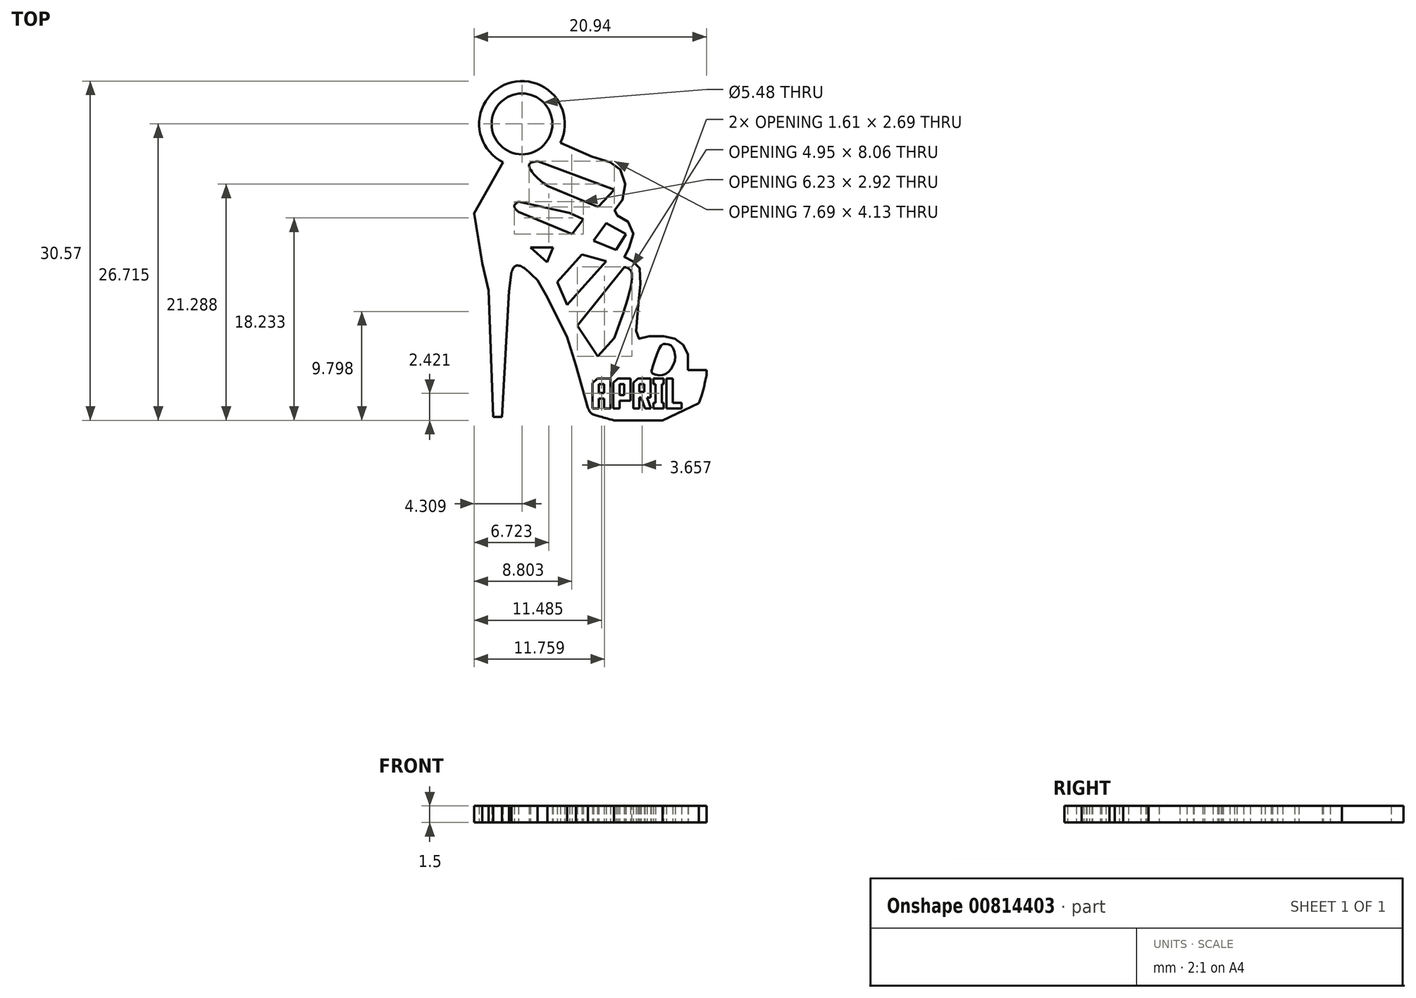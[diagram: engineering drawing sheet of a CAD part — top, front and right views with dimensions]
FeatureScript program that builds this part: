
annotation { "Feature Type Name" : "Feature", "Feature Type Description" : "" }
export const myFeature = defineFeature(function(context is Context, id is Id, definition is map)
    precondition{}
    {
        {
            var Q0;
            Q0=qCreatedBy(makeId("Top.planeOp"),FACE);
            var sketch = newSketch(context, id + "F0", { "sketchPlane" : qUnion([Q0])});
            skLineSegment(sketch, "E0", {"start": v(-16.68, 3.96) * mm, "end": v(-15.9, 3.96) * mm});
            skLineSegment(sketch, "E1", {"start": v(-15.9, 3.96) * mm, "end": v(-15.26, 15.28) * mm});
            skLineSegment(sketch, "E2", {"start": v(-15.26, 15.28) * mm, "end": v(-15.01, 17.04) * mm});
            skFitSpline(sketch, "E3", {"points": [v(-15.01, 17.04) * mm, v(-14.7, 17.54) * mm, v(-14.13, 17.51) * mm, v(-13.22, 16.79) * mm], "startDerivative": vector(0.84, 2.09) * mm, "endDerivative": vector(2.2, -2.1) * mm});
            skLineSegment(sketch, "E4", {"start": v(-13.22, 16.79) * mm, "end": v(-12.7, 16.29) * mm});
            skLineSegment(sketch, "E5", {"start": v(-12.7, 16.29) * mm, "end": v(-11.78, 14.72) * mm});
            skLineSegment(sketch, "E6", {"start": v(-11.78, 14.72) * mm, "end": v(-10.03, 11.14) * mm});
            skLineSegment(sketch, "E7", {"start": v(-10.03, 11.14) * mm, "end": v(-9.2, 8.6) * mm});
            skLineSegment(sketch, "E8", {"start": v(-9.2, 8.6) * mm, "end": v(-8.13, 4.75) * mm});
            skFitSpline(sketch, "E9", {"points": [v(-8.13, 4.75) * mm, v(-7.86, 4.3) * mm, v(-7.32, 4.07) * mm, v(-5.8, 3.65) * mm], "startDerivative": vector(0.86, -1.92) * mm, "endDerivative": vector(3.7, -1) * mm});
            skLineSegment(sketch, "E10", {"start": v(-5.8, 3.65) * mm, "end": v(-3.32, 3.65) * mm});
            skLineSegment(sketch, "E11", {"start": v(-3.32, 3.65) * mm, "end": v(-1.41, 3.65) * mm});
            skLineSegment(sketch, "E12", {"start": v(-1.41, 3.65) * mm, "end": v(0.53, 4.57) * mm});
            skLineSegment(sketch, "E13", {"start": v(0.53, 4.57) * mm, "end": v(1.87, 5.2) * mm});
            skLineSegment(sketch, "E14", {"start": v(2.55, 7.7) * mm, "end": v(2.55, 8.18) * mm});
            skLineSegment(sketch, "E15", {"start": v(2.55, 8.18) * mm, "end": v(0.87, 8.18) * mm});
            skFitSpline(sketch, "E16", {"points": [v(0.87, 8.95) * mm, v(0.87, 9.57) * mm, v(0.2, 10.71) * mm, v(-0.94, 11.17) * mm, v(-3.14, 11.12) * mm, v(-3.7, 11.05) * mm, v(-3.4, 16.13) * mm, v(-3.9, 17.9) * mm, v(-4.83, 18.34) * mm, v(-4.12, 19.88) * mm, v(-4.72, 21.75) * mm, v(-5.82, 22.35) * mm, v(-4.97, 23.62) * mm, v(-5.27, 26.34) * mm, v(-10.61, 28.67) * mm], "startDerivative": vector(2.17, 13.71) * mm, "endDerivative": vector(-80.97, 44.17) * mm});
            skLineSegment(sketch, "E17", {"start": v(-15.8, 26.9) * mm, "end": v(-18.4, 22.3) * mm});
            skLineSegment(sketch, "E18", {"start": v(-18.4, 22.3) * mm, "end": v(-17.67, 17.78) * mm});
            skLineSegment(sketch, "E19", {"start": v(-17.67, 17.78) * mm, "end": v(-17.1, 15.35) * mm});
            skLineSegment(sketch, "E20", {"start": v(-17.1, 15.35) * mm, "end": v(-16.68, 3.96) * mm});
            skLineSegment(sketch, "E21", {"start": v(-12.7, 27) * mm, "end": v(-5.74, 24.42) * mm});
            skLineSegment(sketch, "E22", {"start": v(-5.74, 24.42) * mm, "end": v(-7.22, 22.87) * mm});
            skLineSegment(sketch, "E23", {"start": v(-7.22, 22.87) * mm, "end": v(-11.82, 24.8) * mm});
            skFitSpline(sketch, "E24", {"points": [v(-11.82, 24.8) * mm, v(-13, 25.82) * mm, v(-13.43, 26.72) * mm, v(-12.7, 27) * mm], "startDerivative": vector(-3.15, 2.36) * mm, "endDerivative": vector(3.5, 0.55) * mm});
            skLineSegment(sketch, "E25", {"start": v(-9.78, 22.33) * mm, "end": v(-8.55, 21.75) * mm});
            skLineSegment(sketch, "E26", {"start": v(-8.55, 21.75) * mm, "end": v(-9.55, 20.42) * mm});
            skLineSegment(sketch, "E27", {"start": v(-9.55, 20.42) * mm, "end": v(-14.4, 22.43) * mm});
            skFitSpline(sketch, "E28", {"points": [v(-14.4, 22.43) * mm, v(-14.78, 22.96) * mm, v(-14.4, 23.34) * mm], "startDerivative": vector(-1.1, 1.06) * mm, "endDerivative": vector(1.14, 0.76) * mm});
            skLineSegment(sketch, "E29", {"start": v(-14.4, 23.34) * mm, "end": v(-9.78, 22.33) * mm});
            skLineSegment(sketch, "E30", {"start": v(-6.48, 21.42) * mm, "end": v(-7.62, 19.83) * mm});
            skLineSegment(sketch, "E31", {"start": v(-7.62, 19.83) * mm, "end": v(-5.6, 19) * mm});
            skLineSegment(sketch, "E32", {"start": v(-5.6, 19) * mm, "end": v(-4.72, 20.42) * mm});
            skLineSegment(sketch, "E33", {"start": v(-4.72, 20.42) * mm, "end": v(-6.48, 21.42) * mm});
            skLineSegment(sketch, "E34", {"start": v(-13.3, 19.22) * mm, "end": v(-11.29, 19.22) * mm});
            skLineSegment(sketch, "E35", {"start": v(-11.29, 19.22) * mm, "end": v(-11.83, 17.9) * mm});
            skLineSegment(sketch, "E36", {"start": v(-11.83, 17.9) * mm, "end": v(-13.3, 19.22) * mm});
            skLineSegment(sketch, "E37", {"start": v(-10.9, 16.13) * mm, "end": v(-8.69, 18.6) * mm});
            skLineSegment(sketch, "E38", {"start": v(-8.69, 18.6) * mm, "end": v(-6.48, 17.98) * mm});
            skLineSegment(sketch, "E39", {"start": v(-6.48, 17.98) * mm, "end": v(-10, 14.06) * mm});
            skLineSegment(sketch, "E40", {"start": v(-10, 14.06) * mm, "end": v(-10.9, 16.13) * mm});
            skLineSegment(sketch, "E41", {"start": v(-4.83, 17.48) * mm, "end": v(-9.1, 12.2) * mm});
            skLineSegment(sketch, "E42", {"start": v(-9.1, 12.2) * mm, "end": v(-7.24, 9.42) * mm});
            skLineSegment(sketch, "E43", {"start": v(-7.24, 9.42) * mm, "end": v(-5.76, 11.06) * mm});
            skFitSpline(sketch, "E44", {"points": [v(-5.76, 11.06) * mm, v(-4.21, 17) * mm, v(-4.83, 17.48) * mm], "startDerivative": vector(3.76, 10.36) * mm, "endDerivative": vector(-2.95, 0.99) * mm});
            skFitSpline(sketch, "E45", {"points": [v(-1.53, 10.4) * mm, v(-2.31, 8.42) * mm, v(-2.37, 7.92) * mm, v(-1.62, 7.7) * mm, v(-0.9, 8.01) * mm, v(-0.28, 9.14) * mm, v(-0.6, 10.35) * mm, v(-1.12, 10.54) * mm, v(-1.53, 10.4) * mm]});
            skArc(sketch, "E46", {"start": v(-10.61, 28.67) * mm, "mid": v(-15.32, 34.02) * mm, "end": v(-15.8, 26.9) * mm});
            skLineSegment(sketch, "E47", {"start": v(0.87, 8.95) * mm, "end": v(0.87, 8.18) * mm});
            skCircle(sketch, "E48", {"center": v(-14.08, 30.36) * mm, "radius": 2.74 * mm});
            skFitSpline(sketch, "E49", {"points": [v(1.87, 5.2) * mm, v(2.18, 6.1) * mm, v(2.55, 7.7) * mm], "startDerivative": vector(0.73, 1.92) * mm, "endDerivative": vector(0.65, 3.04) * mm});
            skSolve(sketch);
        }
        {
            var Q0;
            Q0=qCreatedBy(makeId("Top.planeOp"),FACE);
            var sketch = newSketch(context, id + "F1", { "sketchPlane" : qUnion([Q0])});
            skLineSegment(sketch, "E50", {"start": v(-7.14, 4.73) * mm, "end": v(-7.7, 4.73) * mm});
            skLineSegment(sketch, "E51", {"start": v(-7.7, 4.73) * mm, "end": v(-7.7, 6.99) * mm});
            skLineSegment(sketch, "E52", {"start": v(-7.7, 6.99) * mm, "end": v(-7.28, 7.41) * mm});
            skLineSegment(sketch, "E53", {"start": v(-7.28, 7.41) * mm, "end": v(-6.1, 7.41) * mm});
            skLineSegment(sketch, "E54", {"start": v(-6.1, 7.41) * mm, "end": v(-6.1, 4.73) * mm});
            skLineSegment(sketch, "E55", {"start": v(-6.1, 4.73) * mm, "end": v(-6.66, 4.73) * mm});
            skLineSegment(sketch, "E56", {"start": v(-6.66, 4.73) * mm, "end": v(-6.66, 5.6) * mm});
            skLineSegment(sketch, "E57", {"start": v(-6.66, 5.6) * mm, "end": v(-7.14, 5.6) * mm});
            skLineSegment(sketch, "E58", {"start": v(-7.14, 5.6) * mm, "end": v(-7.14, 4.73) * mm});
            skLineSegment(sketch, "E59", {"start": v(-6.66, 6.12) * mm, "end": v(-6.66, 6.9) * mm});
            skLineSegment(sketch, "E60", {"start": v(-6.66, 6.9) * mm, "end": v(-7.14, 6.9) * mm});
            skLineSegment(sketch, "E61", {"start": v(-7.14, 6.9) * mm, "end": v(-7.14, 6.12) * mm});
            skLineSegment(sketch, "E62", {"start": v(-7.14, 6.12) * mm, "end": v(-6.66, 6.12) * mm});
            skLineSegment(sketch, "E63", {"start": v(-5.29, 4.73) * mm, "end": v(-5.85, 4.73) * mm});
            skLineSegment(sketch, "E64", {"start": v(-5.85, 4.73) * mm, "end": v(-5.85, 7.03) * mm});
            skLineSegment(sketch, "E65", {"start": v(-5.85, 7.03) * mm, "end": v(-5.44, 7.41) * mm});
            skLineSegment(sketch, "E66", {"start": v(-5.44, 7.41) * mm, "end": v(-4.3, 7.41) * mm});
            skLineSegment(sketch, "E67", {"start": v(-4.3, 7.41) * mm, "end": v(-4.3, 5.4) * mm});
            skLineSegment(sketch, "E68", {"start": v(-4.3, 5.4) * mm, "end": v(-5.29, 5.4) * mm});
            skLineSegment(sketch, "E69", {"start": v(-5.29, 5.4) * mm, "end": v(-5.29, 4.73) * mm});
            skLineSegment(sketch, "E70", {"start": v(-4.86, 5.92) * mm, "end": v(-4.86, 6.9) * mm});
            skLineSegment(sketch, "E71", {"start": v(-4.86, 6.9) * mm, "end": v(-5.29, 6.9) * mm});
            skLineSegment(sketch, "E72", {"start": v(-5.29, 6.9) * mm, "end": v(-5.29, 5.92) * mm});
            skLineSegment(sketch, "E73", {"start": v(-5.29, 5.92) * mm, "end": v(-4.86, 5.92) * mm});
            skLineSegment(sketch, "E74", {"start": v(-3, 4.73) * mm, "end": v(-3.34, 5.7) * mm});
            skLineSegment(sketch, "E75", {"start": v(-3.34, 5.7) * mm, "end": v(-3.5, 5.7) * mm});
            skLineSegment(sketch, "E76", {"start": v(-3.5, 5.7) * mm, "end": v(-3.5, 4.73) * mm});
            skLineSegment(sketch, "E77", {"start": v(-3.5, 4.73) * mm, "end": v(-4.05, 4.73) * mm});
            skLineSegment(sketch, "E78", {"start": v(-4.05, 4.73) * mm, "end": v(-4.05, 7.03) * mm});
            skLineSegment(sketch, "E79", {"start": v(-4.05, 7.03) * mm, "end": v(-3.64, 7.41) * mm});
            skLineSegment(sketch, "E80", {"start": v(-3.64, 7.41) * mm, "end": v(-2.5, 7.41) * mm});
            skLineSegment(sketch, "E81", {"start": v(-2.5, 7.41) * mm, "end": v(-2.5, 5.7) * mm});
            skLineSegment(sketch, "E82", {"start": v(-2.5, 5.7) * mm, "end": v(-2.8, 5.7) * mm});
            skLineSegment(sketch, "E83", {"start": v(-2.8, 5.7) * mm, "end": v(-2.44, 4.73) * mm});
            skLineSegment(sketch, "E84", {"start": v(-2.44, 4.73) * mm, "end": v(-3, 4.73) * mm});
            skLineSegment(sketch, "E85", {"start": v(-3.06, 6.2) * mm, "end": v(-3.06, 6.9) * mm});
            skLineSegment(sketch, "E86", {"start": v(-3.06, 6.9) * mm, "end": v(-3.5, 6.9) * mm});
            skLineSegment(sketch, "E87", {"start": v(-3.5, 6.9) * mm, "end": v(-3.5, 6.2) * mm});
            skLineSegment(sketch, "E88", {"start": v(-3.5, 6.2) * mm, "end": v(-3.06, 6.2) * mm});
            skLineSegment(sketch, "E89", {"start": v(-1.3, 5.24) * mm, "end": v(-1.3, 4.73) * mm});
            skLineSegment(sketch, "E90", {"start": v(-1.3, 4.73) * mm, "end": v(-2.23, 4.73) * mm});
            skLineSegment(sketch, "E91", {"start": v(-2.23, 4.73) * mm, "end": v(-2.23, 5.24) * mm});
            skLineSegment(sketch, "E92", {"start": v(-2.23, 5.24) * mm, "end": v(-2.05, 5.24) * mm});
            skLineSegment(sketch, "E93", {"start": v(-2.05, 5.24) * mm, "end": v(-2.05, 6.9) * mm});
            skLineSegment(sketch, "E94", {"start": v(-2.05, 6.9) * mm, "end": v(-2.23, 6.9) * mm});
            skLineSegment(sketch, "E95", {"start": v(-2.23, 6.9) * mm, "end": v(-2.23, 7.41) * mm});
            skLineSegment(sketch, "E96", {"start": v(-2.23, 7.41) * mm, "end": v(-1.3, 7.41) * mm});
            skLineSegment(sketch, "E97", {"start": v(-1.3, 7.41) * mm, "end": v(-1.3, 6.9) * mm});
            skLineSegment(sketch, "E98", {"start": v(-1.3, 6.9) * mm, "end": v(-1.49, 6.9) * mm});
            skLineSegment(sketch, "E99", {"start": v(-1.49, 6.9) * mm, "end": v(-1.49, 5.24) * mm});
            skLineSegment(sketch, "E100", {"start": v(-1.49, 5.24) * mm, "end": v(-1.3, 5.24) * mm});
            skLineSegment(sketch, "E101", {"start": v(-1.06, 4.73) * mm, "end": v(-1.06, 7.41) * mm});
            skLineSegment(sketch, "E102", {"start": v(-1.06, 7.41) * mm, "end": v(-0.5, 7.41) * mm});
            skLineSegment(sketch, "E103", {"start": v(-0.5, 7.41) * mm, "end": v(-0.5, 5.24) * mm});
            skLineSegment(sketch, "E104", {"start": v(-0.5, 5.24) * mm, "end": v(0.3, 5.24) * mm});
            skLineSegment(sketch, "E105", {"start": v(0.3, 5.24) * mm, "end": v(0.3, 4.73) * mm});
            skLineSegment(sketch, "E106", {"start": v(0.3, 4.73) * mm, "end": v(-1.06, 4.73) * mm});
            skSolve(sketch);
        }
        {
            var Q0;
            Q0 = qSketchRegion(id + "F0", true);
            extrude(context, id + "F2", {"entities" : qUnion([Q0]), "depth" : 1.5 * mm, "offsetDistance" : 25.4 * mm});
        }
        {
            var Q0;
            Q0 = qSketchRegion(id + "F1", true);
            extrude(context, id + "F3", {"entities" : qUnion([Q0]), "operationType" : NewBodyOperationType.REMOVE, "depth" : 25.4 * mm, "offsetDistance" : 25.4 * mm});
        }
    });
